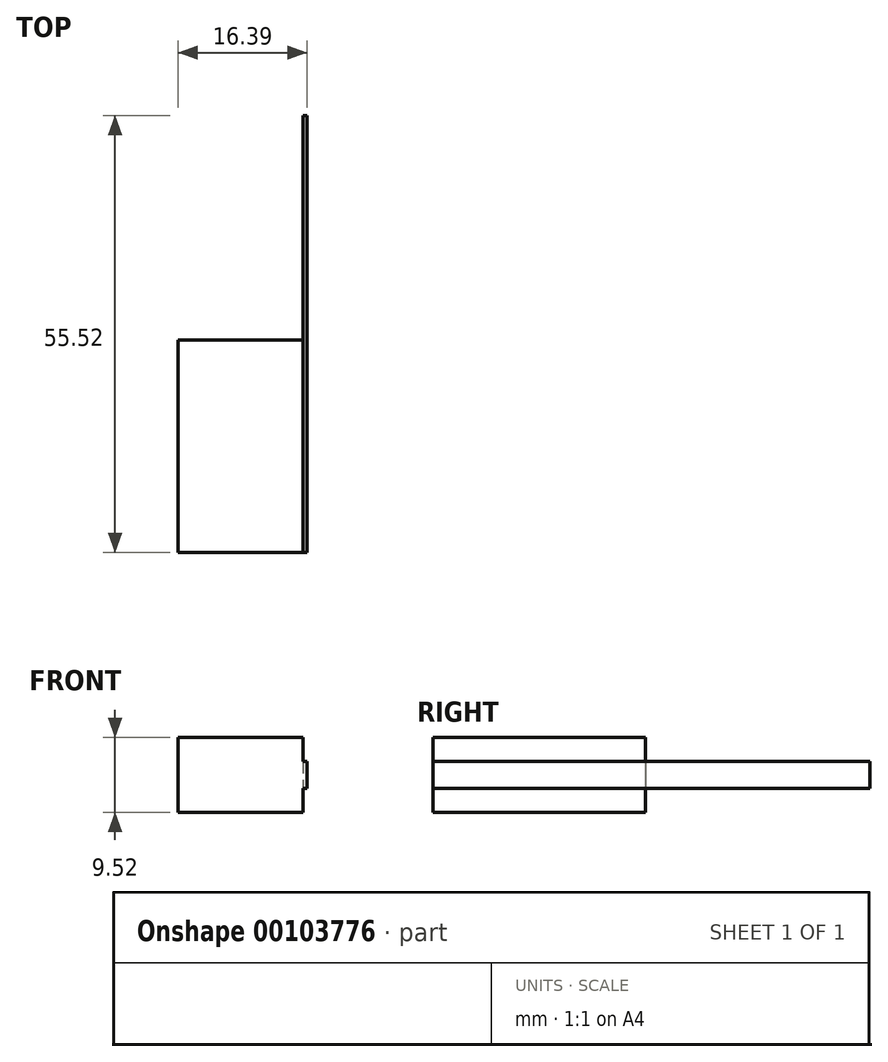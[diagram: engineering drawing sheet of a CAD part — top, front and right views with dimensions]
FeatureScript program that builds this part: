
annotation { "Feature Type Name" : "Feature", "Feature Type Description" : "" }
export const myFeature = defineFeature(function(context is Context, id is Id, definition is map)
    precondition{}
    {
        {
            var Q0;
            Q0=qCreatedBy(makeId("Front.planeOp"),FACE);
            var sketch = newSketch(context, id + "F0", { "sketchPlane" : qUnion([Q0])});
            skLineSegment(sketch, "E0.bottom", {"start": v(7.94, 4.76) * mm, "end": v(-7.94, 4.76) * mm});
            skLineSegment(sketch, "E0.top", {"start": v(7.94, -4.76) * mm, "end": v(-7.94, -4.76) * mm});
            skLineSegment(sketch, "E0.left", {"start": v(7.94, 4.76) * mm, "end": v(7.94, -4.76) * mm});
            skLineSegment(sketch, "E0.right", {"start": v(-7.94, 4.76) * mm, "end": v(-7.94, -4.76) * mm});
            skPoint(sketch, "E0.middle", {"position": v(0, 0) * mm});
            skSolve(sketch);
        }
        {
            var Q0;
            Q0=makeQuery(id+"F0.imprint","IMPRINT",FACE,{"disambiguationData":[TD([[makeQuery(id+"F0.imprint","IMPRINT",EDGE,{"derivedFrom":sQuery(id+"F0.wireOp",EDGE,"E0.bottom")}),1.0]])]});
            extrude(context, id + "F1", {"entities" : qUnion([Q0]), "depth" : 26.99 * mm});
        }
        {
            var Q0;
            Q0=makeQuery(id+"F1.opExtrude","SWEPT_FACE",FACE,{"disambiguationData":[OSD([sQuery(id+"F0.wireOp",EDGE,"E0.left")])]});
            var sketch = newSketch(context, id + "F2", { "sketchPlane" : qUnion([Q0])});
            skLineSegment(sketch, "E1", {"start": v(-26.99, 0) * mm, "end": v(0, 0) * mm});
            skLineSegment(sketch, "E2", {"start": v(-26.99, 0) * mm, "end": v(-26.99, 1.7) * mm});
            skLineSegment(sketch, "E3.bottom", {"start": v(-26.99, 0) * mm, "end": v(28.53, 0) * mm});
            skLineSegment(sketch, "E3.top", {"start": v(-26.99, 1.7) * mm, "end": v(28.53, 1.7) * mm});
            skLineSegment(sketch, "E3.right", {"start": v(28.53, 0) * mm, "end": v(28.53, 1.7) * mm});
            skLineSegment(sketch, "E4.MirrorCS", {"start": v(-26.99, -1.7) * mm, "end": v(28.53, -1.7) * mm});
            skLineSegment(sketch, "E5.MirrorCS", {"start": v(-26.99, 0) * mm, "end": v(-26.99, -1.7) * mm});
            skLineSegment(sketch, "E6.MirrorCS", {"start": v(28.53, 0) * mm, "end": v(28.53, -1.7) * mm});
            skSolve(sketch);
        }
        {
            var Q0;
            {var subQ0=sQuery(id+"F2.wireOp",EDGE,"E3.right");Q0=makeQuery(id+"F2.imprint","IMPRINT",FACE,{"disambiguationData":[TD([[makeQuery(id+"F2.imprint","IMPRINT",EDGE,{"derivedFrom":subQ0}),1.0]])]});}
            var Q1;
            {var subQ0=sQuery(id+"F2.wireOp",EDGE,"E2");Q1=makeQuery(id+"F2.imprint","IMPRINT",FACE,{"disambiguationData":[TD([[makeQuery(id+"F2.imprint","IMPRINT",EDGE,{"derivedFrom":subQ0}),1.0]])]});}
            var Q2;
            {var subQ0=sQuery(id+"F2.wireOp",EDGE,"E5.MirrorCS");Q2=makeQuery(id+"F2.imprint","IMPRINT",FACE,{"disambiguationData":[TD([[makeQuery(id+"F2.imprint","IMPRINT",EDGE,{"derivedFrom":subQ0}),1.0]])]});}
            var Q3;
            {var subQ0=sQuery(id+"F2.wireOp",EDGE,"E6.MirrorCS");Q3=makeQuery(id+"F2.imprint","IMPRINT",FACE,{"disambiguationData":[TD([[makeQuery(id+"F2.imprint","IMPRINT",EDGE,{"derivedFrom":subQ0}),-1.0]])]});}
            extrude(context, id + "F3", {"entities" : qUnion([Q0, Q1, Q2, Q3]), "operationType" : NewBodyOperationType.ADD, "depth" : 0.5 * mm});
        }
    });
